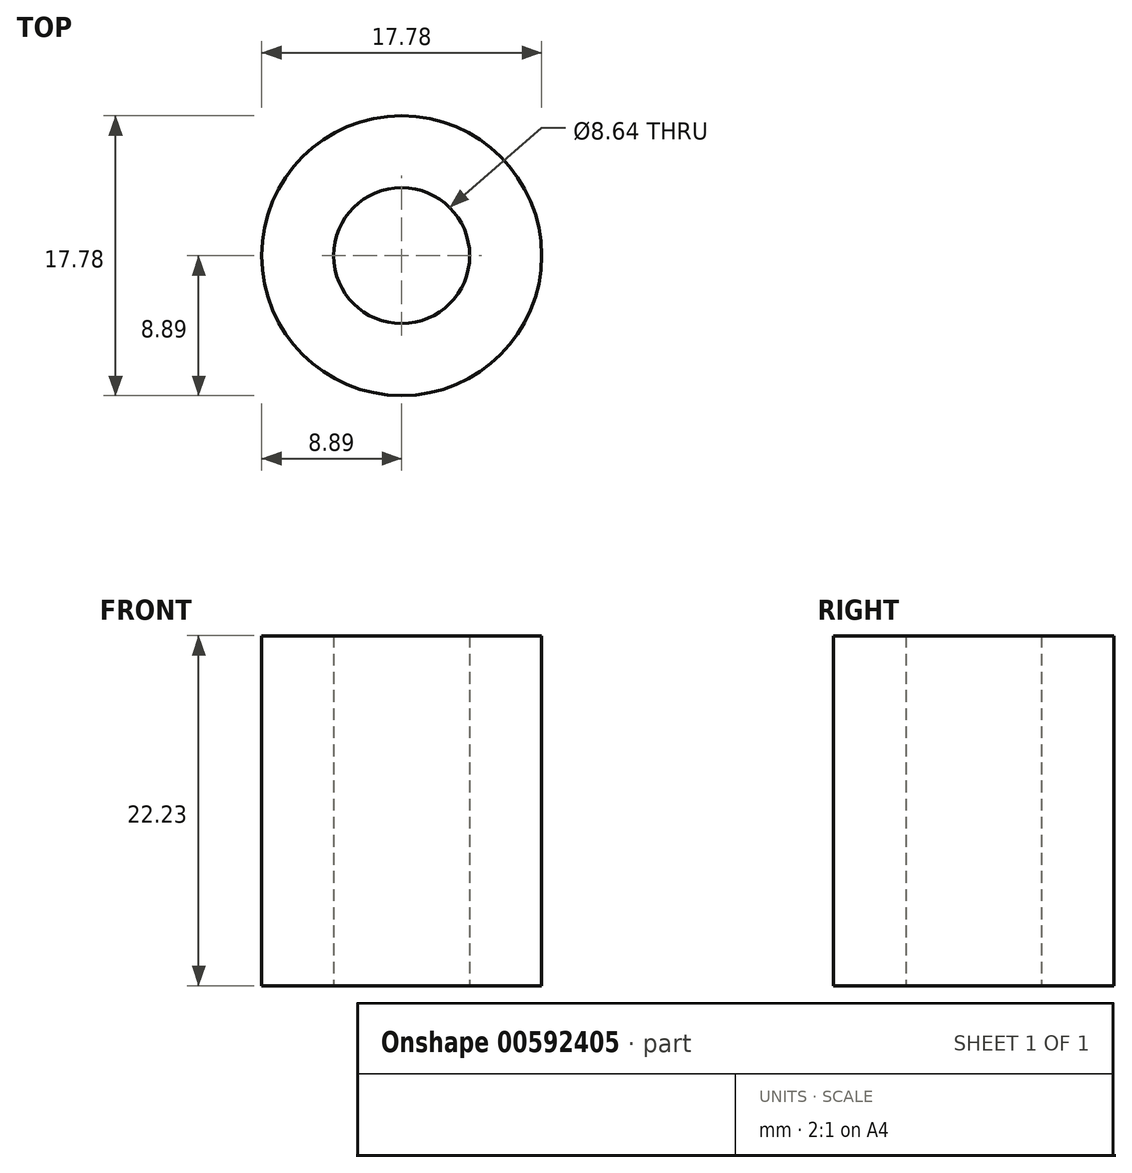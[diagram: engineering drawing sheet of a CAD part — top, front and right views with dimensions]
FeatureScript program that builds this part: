
annotation { "Feature Type Name" : "Feature", "Feature Type Description" : "" }
export const myFeature = defineFeature(function(context is Context, id is Id, definition is map)
    precondition{}
    {
        {
            var Q0;
            Q0=qCreatedBy(makeId("Top.planeOp"),FACE);
            var sketch = newSketch(context, id + "F0", { "sketchPlane" : qUnion([Q0])});
            skCircle(sketch, "E0", {"center": v(0, 0) * mm, "radius": 8.9 * mm});
            skCircle(sketch, "E1", {"center": v(0, 0) * mm, "radius": 4.32 * mm});
            skSolve(sketch);
        }
        {
            var Q0;
            Q0 = qSketchRegion(id + "F0", true);
            extrude(context, id + "F1", {"entities" : qUnion([Q0]), "depth" : 22.22 * mm, "offsetDistance" : 25.4 * mm});
        }
    });
